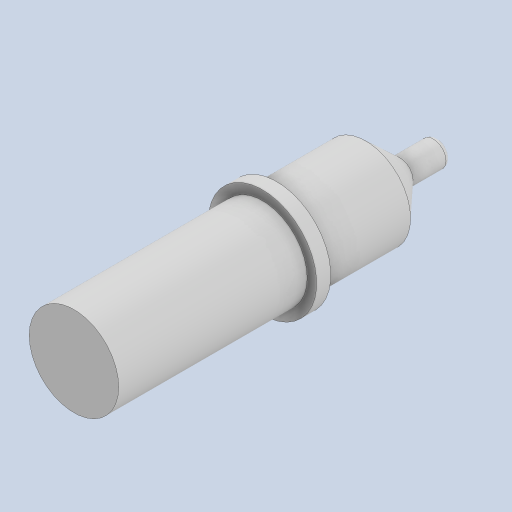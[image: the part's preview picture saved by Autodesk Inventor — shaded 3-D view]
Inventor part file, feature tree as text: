
AUTODESK INVENTOR PART (.ipt)
format: ipt  version: 2024 (Build 280153000, 153)  size: 134,656 bytes
history: native  units: mm
features: other x1, revolve x1, fillet x1, sketch x1
ambient origin geometry x8: Origin, YZ Plane, XZ Plane, XY Plane, X Axis, Y Axis, Z Axis, Center Point
bodies: Body1 (feature_tree)
feature tree (4):
  other  "Sólido1"
  revolve  "Revolución1"  [1 undecoded]
  fillet  "Empalme1"  Radius=2.7mm
  sketch  "Boceto1"  dims[d0=9.5mm d1=37.26mm d2=2.7mm d3=8.0mm d4=10.0mm d5=2.0mm d6=3.0mm d7=40.0mm d8=90.0deg d9=1.0mm]
note: 1 required parameter value undecoded (feature->parameter linkage not recoverable at this tier; creation-order binding heuristic only, values carry confidence <= 0.55)
